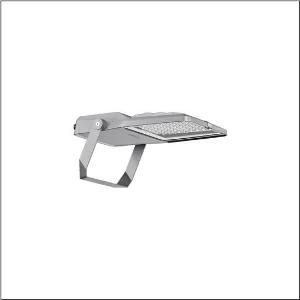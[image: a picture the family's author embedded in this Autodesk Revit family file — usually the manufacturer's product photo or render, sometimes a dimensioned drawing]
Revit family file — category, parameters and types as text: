
# Revit family: floodlight_fl_21_iq_mini___rs12_5xa7771b4b1a_1748
name_source: partatom
category: Lighting Fixtures
units: mm (PartAtom-declared; Revit-internal decimal feet)

## family parameters
Cut with Voids When Loaded = No
Host = Face
Light Source = No
Part Type = Normal
Room Calculation Point = No
Round Connector Dimension = Use Diameter
Shared = No

## types (1)
- --- (1 x LED, 6560 lm, 45.5 W, 4000K)
    Apparent Load = 46 VA
    CIE Flux Codes = 79 92 99 100 100
    Color Rendering = 70
    Color Temperature = 4000K
    Default Elevation = 1800 mm
    Description = Floodlight FL 21 iQ mini, floodlight, primary light control with lens, of PMMA, primary optical cover: protective disc, of toughened safety glass, transparent, light distribution: RS12, light emission: direct distribution, installation type: surface-mounted, lamps: LED, High Power LED, rated values: 6.560lm | 45,5W | 144,2lm/W (begin service life); end service life: 6.560lm | 48W; at 50% lumin. flux: 3.280lm | 21,5W | 152,6lm/W, colour temperature: 4000K, colour rendering: CRI > 70, light colour: 740, light setting 1 begin service life: 100% | 6.560lm | 45,5W | 144,2lm/W | 4.000K, light setting 1 end service life: 48W, further light settings possible, control: Auto-Match, Temp-Guard, Lumen-Switch, Night-Set, Smart-Wire, Light-Fading, Desk-Remote (wireless, voltage-free reading and setting of iQ features in the workshop via application-optimized NFC function/RFID function), optimised constant luminous flux control (CLO 2.0), pre-setting: linear dimming characteristic, with terminal, 6-pole, mains connection: 220..240V, AC, 50/60Hz, luminaire housing, of diecast aluminium, powder-coated, SITECO metallic grey (DB 702S), corrosivity category C5 mid according to DIN EN ISO 12944suitable for swimming poolschlorine-resistant, sealing non-destructively replaceable, mounting bracket, of steel, galvanised, powder-coated, SITECO metallic grey (DB 702S), protection rating (complete): IP66, insulation class (complete): insulation class II (safety insulation), certification: CE, ENEC, VDE, protection symbol: D, impact resistance: IK08, permissible operating ambient temperature: -40..+40°C, permissible operating ambient temperature for outdoor applications: -40..+50°C, standard: DIN EN 12944, LABS conformity tested according to VDMA 24364:2018-05, packaging unit: 1 piece

Light Distribution: RS12
    Height = 70 mm
    Lamp = 1 x LED
    Lamp Light Flux = 6560 lm
    Lamp Power = 45.5 W
    Lamp count = 1
    Length = 485 mm
    Luminous efficacy = 144 lm/W
    Manufacturer = Siteco
    ModVariant = No
    Model = 5XA7771B4B1A
    Mounting Place = Wall
    Mounting Type = Surface mounted
    Number of Poles = 1
    OnlyDefault = Yes
    Power Factor = 1
    Product Name = Floodlight FL 21 iQ mini | RS12
    Product group = floodlight | wall mounted
    ProductGroupID = 2002
    Protection Class = Protection class II
    Protection Degree = IP 66
    RLX_Detail_Level = 1
    RLX_Emergency_Light_Flux = 0 lm
    RLX_Emergency_Type = 0
    RLX_Emergency_Type_DB = No
    RlxData = <blob elided: 91289 chars, md5=cba21cd7>
    Socket = socket
    Standby Power = 0 W
    System Light Flux = 6560 lm
    System Power = 46 W
    Type Comments = factory setting: luminous flux: 100 % | dim-lin: 254 | 463 mA
    Type Image = l_1006845.jpg
    URL = http://relux.com
    VarID = @adj_168993
    Voltage = 0 V
    Weight = 0.00 kg
    Width = 337 mm

## geometry (parser evidence)
native form markers: Blend x4, Sweep x14
no freeform markers — native parametric forms only
